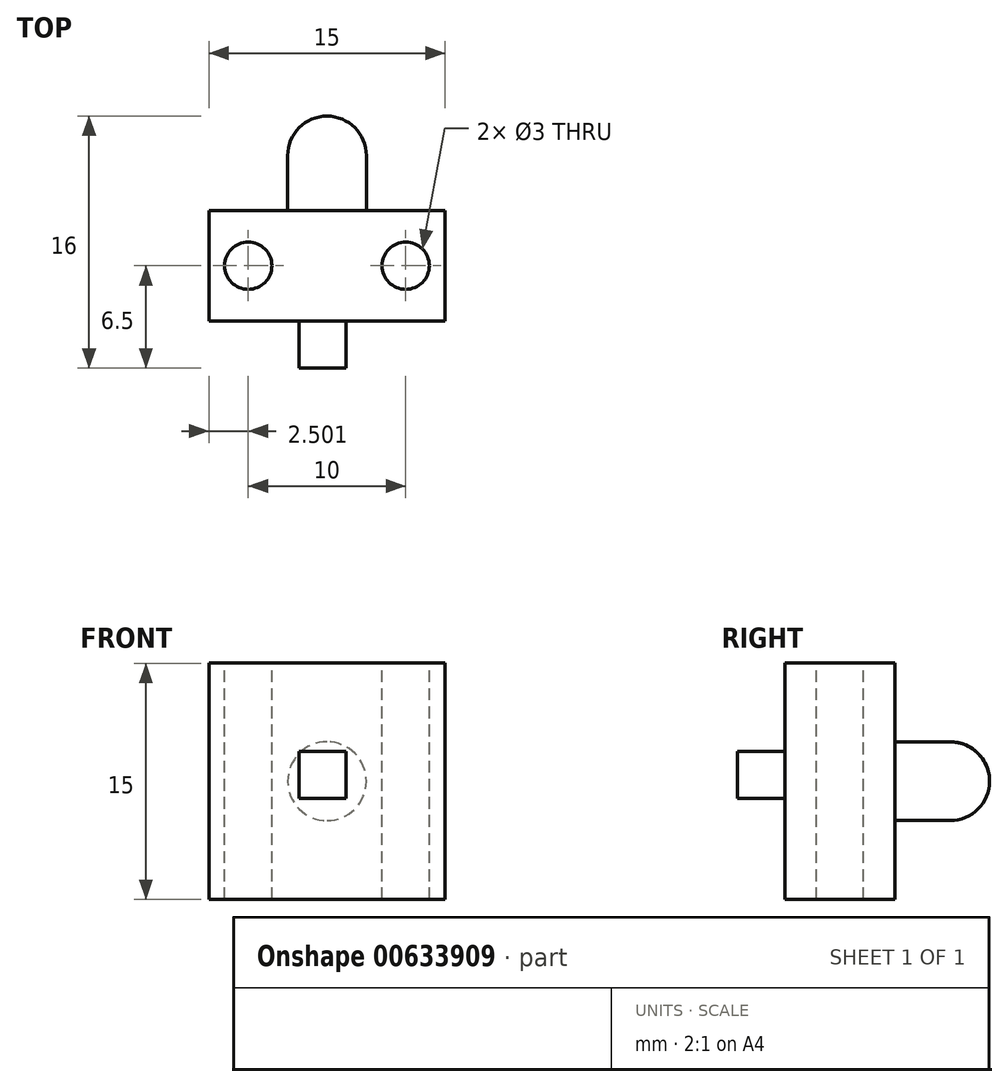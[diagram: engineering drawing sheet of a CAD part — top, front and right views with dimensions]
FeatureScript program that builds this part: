
annotation { "Feature Type Name" : "Feature", "Feature Type Description" : "" }
export const myFeature = defineFeature(function(context is Context, id is Id, definition is map)
    precondition{}
    {
        {
            var Q0;
            Q0=qCreatedBy(makeId("Front.planeOp"),FACE);
            var sketch = newSketch(context, id + "F0", { "sketchPlane" : qUnion([Q0])});
            skLineSegment(sketch, "E0.bottom", {"start": v(-3.14, 10.35) * mm, "end": v(11.86, 10.35) * mm});
            skLineSegment(sketch, "E0.top", {"start": v(-3.14, -4.65) * mm, "end": v(11.86, -4.65) * mm});
            skLineSegment(sketch, "E0.left", {"start": v(-3.14, 10.35) * mm, "end": v(-3.14, -4.65) * mm});
            skLineSegment(sketch, "E0.right", {"start": v(11.86, 10.35) * mm, "end": v(11.86, -4.65) * mm});
            skSolve(sketch);
        }
        {
            var Q0;
            Q0=makeQuery(id+"F0.imprint","IMPRINT",FACE,{"disambiguationData":[TD([[makeQuery(id+"F0.imprint","IMPRINT",EDGE,{"derivedFrom":sQuery(id+"F0.wireOp",EDGE,"E0.bottom")}),-1.0]])]});
            extrude(context, id + "F1", {"entities" : qUnion([Q0]), "depth" : 7 * mm, "offsetDistance" : 25.4 * mm});
        }
        {
            var Q0;
            Q0=makeQuery(id+"F1.opExtrude","SWEPT_FACE",FACE,{"disambiguationData":[OSD([sQuery(id+"F0.wireOp",EDGE,"E0.bottom")])]});
            var sketch = newSketch(context, id + "F2", { "sketchPlane" : qUnion([Q0])});
            skCircle(sketch, "E1", {"center": v(-0.64, -3.5) * mm, "radius": 1.5 * mm});
            skSolve(sketch);
        }
        {
            var Q0;
            Q0=makeQuery(id+"F2.imprint","IMPRINT",FACE,{"disambiguationData":[TD([[makeQuery(id+"F2.imprint","IMPRINT",EDGE,{"derivedFrom":sQuery(id+"F2.wireOp",EDGE,"E1")}),1.0]])]});
            extrude(context, id + "F3", {"entities" : qUnion([Q0]), "operationType" : NewBodyOperationType.REMOVE, "oppositeDirection" : true, "depth" : 15 * mm, "offsetDistance" : 25.4 * mm});
        }
        {
            var Q0;
            Q0=makeQuery(id+"F1.opExtrude","SWEPT_FACE",FACE,{"disambiguationData":[OSD([sQuery(id+"F0.wireOp",EDGE,"E0.bottom")])]});
            var sketch = newSketch(context, id + "F4", { "sketchPlane" : qUnion([Q0])});
            skCircle(sketch, "E2", {"center": v(9.36, -3.5) * mm, "radius": 1.5 * mm});
            skSolve(sketch);
        }
        {
            var Q0;
            Q0=makeQuery(id+"F4.imprint","IMPRINT",FACE,{"disambiguationData":[TD([[makeQuery(id+"F4.imprint","IMPRINT",EDGE,{"derivedFrom":sQuery(id+"F4.wireOp",EDGE,"E2")}),1.0]])]});
            extrude(context, id + "F5", {"entities" : qUnion([Q0]), "operationType" : NewBodyOperationType.REMOVE, "oppositeDirection" : true, "depth" : 15 * mm, "offsetDistance" : 25.4 * mm});
        }
        {
            var Q0;
            Q0=makeQuery(id+"F1.opExtrude","CAP_FACE",FACE,{"disambiguationData":[OSD([sQuery(id+"F0.wireOp",EDGE,"E0.bottom"),sQuery(id+"F0.wireOp",EDGE,"E0.top"),sQuery(id+"F0.wireOp",EDGE,"E0.left"),sQuery(id+"F0.wireOp",EDGE,"E0.right")])],"isStart":false});
            var sketch = newSketch(context, id + "F6", { "sketchPlane" : qUnion([Q0])});
            skLineSegment(sketch, "E3.bottom", {"start": v(2.57, 4.76) * mm, "end": v(5.57, 4.76) * mm});
            skLineSegment(sketch, "E3.top", {"start": v(2.57, 1.76) * mm, "end": v(5.57, 1.76) * mm});
            skLineSegment(sketch, "E3.left", {"start": v(2.57, 4.76) * mm, "end": v(2.57, 1.76) * mm});
            skLineSegment(sketch, "E3.right", {"start": v(5.57, 4.76) * mm, "end": v(5.57, 1.76) * mm});
            skSolve(sketch);
        }
        {
            var Q0;
            Q0=makeQuery(id+"F6.imprint","IMPRINT",FACE,{"disambiguationData":[TD([[makeQuery(id+"F6.imprint","IMPRINT",EDGE,{"derivedFrom":sQuery(id+"F6.wireOp",EDGE,"E3.bottom")}),-1.0]])]});
            extrude(context, id + "F7", {"entities" : qUnion([Q0]), "operationType" : NewBodyOperationType.ADD, "depth" : 3 * mm, "offsetDistance" : 25.4 * mm});
        }
        {
            var Q0;
            Q0=makeQuery(id+"F1.opExtrude","CAP_FACE",FACE,{"disambiguationData":[OSD([sQuery(id+"F0.wireOp",EDGE,"E0.bottom"),sQuery(id+"F0.wireOp",EDGE,"E0.top"),sQuery(id+"F0.wireOp",EDGE,"E0.left"),sQuery(id+"F0.wireOp",EDGE,"E0.right")])],"isStart":true});
            var sketch = newSketch(context, id + "F8", { "sketchPlane" : qUnion([Q0])});
            skCircle(sketch, "E4", {"center": v(-4.36, 2.85) * mm, "radius": 2.5 * mm});
            skSolve(sketch);
        }
        {
            var Q0;
            Q0=makeQuery(id+"F8.imprint","IMPRINT",FACE,{"disambiguationData":[TD([[makeQuery(id+"F8.imprint","IMPRINT",EDGE,{"derivedFrom":sQuery(id+"F8.wireOp",EDGE,"E4")}),1.0]])]});
            extrude(context, id + "F9", {"entities" : qUnion([Q0]), "operationType" : NewBodyOperationType.ADD, "depth" : 6 * mm, "offsetDistance" : 25.4 * mm});
        }
        {
            var Q0;
            Q0=makeQuery(id+"F9.opExtrude","CAP_FACE",FACE,{"disambiguationData":[OSD([sQuery(id+"F8.wireOp",EDGE,"E4")])],"isStart":false});
            fillet(context, id + "F10", {"entities" : qUnion([Q0]), "radius" : 2.5 * mm, "tangentPropagation" : true, "allowEdgeOverflow" : false});
        }
    });
